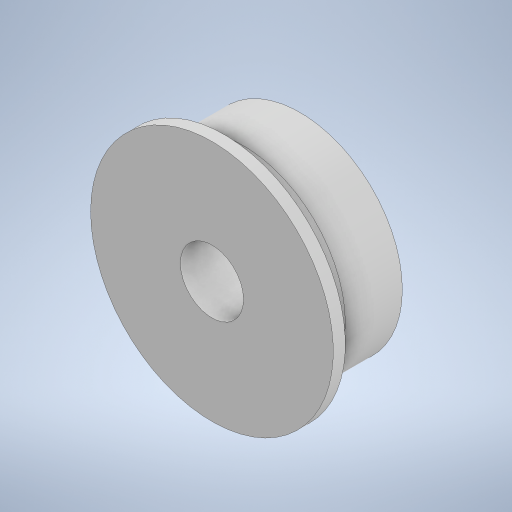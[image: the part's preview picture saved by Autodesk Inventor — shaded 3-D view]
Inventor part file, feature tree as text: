
AUTODESK INVENTOR PART (.ipt)
format: ipt  version: 2023 (Build 270158000, 158)  size: 239,104 bytes
history: native  units: in
note: dims shown in document units (in); Inventor stores cm internally (conversion verified against a paired STEP export)
features: revolve x1, sketch x1
ambient origin geometry x8: Origin, YZ Plane, XZ Plane, XY Plane, X Axis, Y Axis, Z Axis, Center Point
bodies: Solid1 (feature_tree)
feature tree (2):
  revolve  "Revolution1"  [1 undecoded]
  sketch  "Sketch1"  dims[d5=360.0deg]
note: 1 required parameter value undecoded (feature->parameter linkage not recoverable at this tier; creation-order binding heuristic only, values carry confidence <= 0.55)
